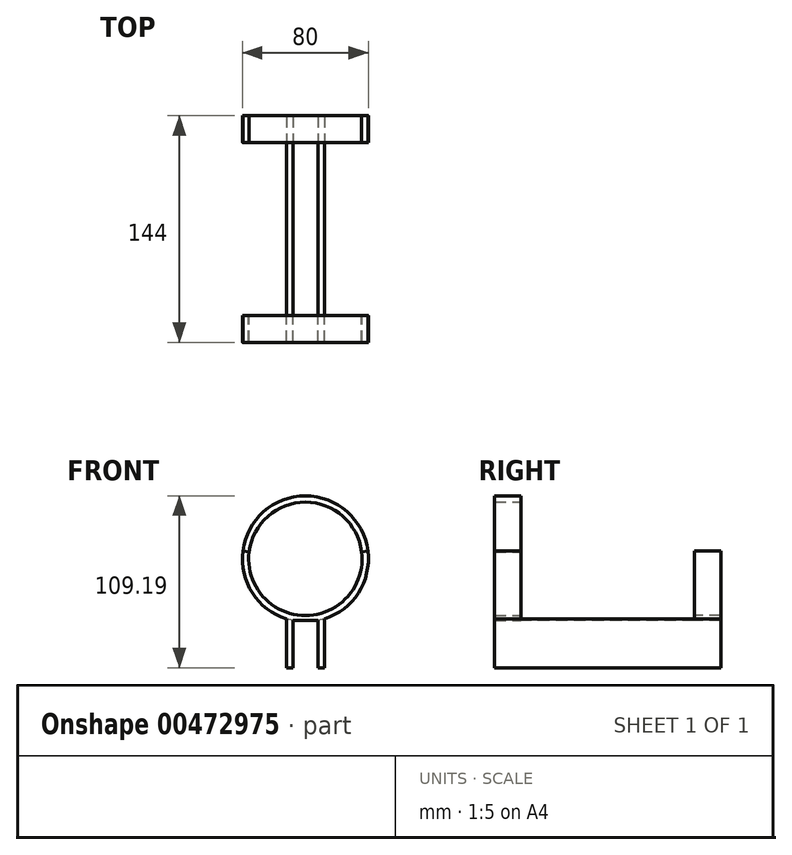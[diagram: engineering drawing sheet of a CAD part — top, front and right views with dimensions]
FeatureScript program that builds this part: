
annotation { "Feature Type Name" : "Feature", "Feature Type Description" : "" }
export const myFeature = defineFeature(function(context is Context, id is Id, definition is map)
    precondition{}
    {
        {
            var Q0;
            Q0=qCreatedBy(makeId("Front.planeOp"),FACE);
            var sketch = newSketch(context, id + "F0", { "sketchPlane" : qUnion([Q0])});
            skArc(sketch, "E0", {"start": v(-35.72, 4.5) * mm, "mid": v(0, -36) * mm, "end": v(35.72, 4.5) * mm});
            skArc(sketch, "E1.0", {"start": v(-39.69, 5) * mm, "mid": v(-33.67, -21.6) * mm, "end": v(-12, -38.16) * mm});
            skLineSegment(sketch, "E2", {"start": v(0, 47.34) * mm, "end": v(0, -79.2) * mm, "construction": true});
            skLineSegment(sketch, "E3", {"start": v(-35.72, 4.5) * mm, "end": v(-39.69, 5) * mm});
            skLineSegment(sketch, "E4.MirrorCS", {"start": v(35.72, 4.5) * mm, "end": v(39.69, 5) * mm});
            skLineSegment(sketch, "E5", {"start": v(8, -39.2) * mm, "end": v(8, -69.2) * mm});
            skLineSegment(sketch, "E6", {"start": v(8, -69.2) * mm, "end": v(12, -69.2) * mm});
            skLineSegment(sketch, "E7", {"start": v(12, -69.2) * mm, "end": v(12, -38.16) * mm});
            skLineSegment(sketch, "E8.MirrorCS", {"start": v(-8, -39.2) * mm, "end": v(-8, -69.2) * mm});
            skLineSegment(sketch, "E9.MirrorCS", {"start": v(-12, -69.2) * mm, "end": v(-12, -38.16) * mm});
            skLineSegment(sketch, "E10.MirrorCS", {"start": v(-8, -69.2) * mm, "end": v(-12, -69.2) * mm});
            skPoint(sketch, "E11.MirrorCS.start.orphan", {"position": v(0, -40) * mm});
            skArc(sketch, "E12.trimOffspring", {"start": v(12, -38.16) * mm, "mid": v(33.67, -21.6) * mm, "end": v(39.69, 5) * mm});
            skLineSegment(sketch, "E13", {"start": v(-8, -39.2) * mm, "end": v(8, -39.2) * mm});
            skArc(sketch, "E14", {"start": v(35.72, 4.5) * mm, "mid": v(0, 36) * mm, "end": v(-35.72, 4.5) * mm});
            skArc(sketch, "E15", {"start": v(39.69, 5) * mm, "mid": v(0, 40) * mm, "end": v(-39.69, 5) * mm});
            skSolve(sketch);
        }
        {
            var Q0;
            Q0=makeQuery(id+"F0.imprint","IMPRINT",FACE,{"disambiguationData":[TD([[makeQuery(id+"F0.imprint","IMPRINT",EDGE,{"derivedFrom":sQuery(id+"F0.wireOp",EDGE,"E0")}),-1.0]])]});
            var sketch = newSketch(context, id + "F1", { "sketchPlane" : qUnion([Q0])});
            skLineSegment(sketch, "E16.0.0", {"start": v(-8, -39.2) * mm, "end": v(8, -39.2) * mm});
            skLineSegment(sketch, "E16.0.1", {"start": v(8, -39.2) * mm, "end": v(8, -69.2) * mm});
            skLineSegment(sketch, "E16.0.2", {"start": v(8, -69.2) * mm, "end": v(12, -69.2) * mm});
            skLineSegment(sketch, "E16.0.3", {"start": v(12, -69.2) * mm, "end": v(12, -38.16) * mm});
            skArc(sketch, "E16.0.4", {"start": v(12, -38.16) * mm, "mid": v(33.67, -21.6) * mm, "end": v(39.69, 5) * mm});
            skLineSegment(sketch, "E16.0.5", {"start": v(39.69, 5) * mm, "end": v(35.72, 4.5) * mm});
            skArc(sketch, "E16.0.6", {"start": v(35.72, 4.5) * mm, "mid": v(0, -36) * mm, "end": v(-35.72, 4.5) * mm});
            skLineSegment(sketch, "E16.0.7", {"start": v(-35.72, 4.5) * mm, "end": v(-39.69, 5) * mm});
            skArc(sketch, "E16.0.8", {"start": v(-39.69, 5) * mm, "mid": v(-33.67, -21.6) * mm, "end": v(-12, -38.16) * mm});
            skLineSegment(sketch, "E16.0.9", {"start": v(-12, -38.16) * mm, "end": v(-12, -69.2) * mm});
            skLineSegment(sketch, "E16.0.10", {"start": v(-12, -69.2) * mm, "end": v(-8, -69.2) * mm});
            skLineSegment(sketch, "E16.0.11", {"start": v(-8, -69.2) * mm, "end": v(-8, -39.2) * mm});
            skSolve(sketch);
        }
        {
            var Q0;
            Q0 = qSketchRegion(id + "F1", true);
            var Q1;
            Q1=makeQuery(id+"F0.imprint","IMPRINT",FACE,{"disambiguationData":[TD([[makeQuery(id+"F0.imprint","IMPRINT",EDGE,{"derivedFrom":sQuery(id+"F0.wireOp",EDGE,"E3")}),-1.0]])]});
            extrude(context, id + "F2", {"entities" : qUnion([Q0, Q1]), "depth" : 17 * mm});
        }
        {
            var Q0;
            Q0=qCreatedBy(makeId("Front.planeOp"),FACE);
            var sketch = newSketch(context, id + "F3", { "sketchPlane" : qUnion([Q0])});
            skLineSegment(sketch, "E17.0", {"start": v(12, -69.2) * mm, "end": v(12, -38.16) * mm});
            skLineSegment(sketch, "E18.0", {"start": v(8, -39.2) * mm, "end": v(8, -69.2) * mm});
            skLineSegment(sketch, "E19.0", {"start": v(8, -69.2) * mm, "end": v(12, -69.2) * mm});
            skLineSegment(sketch, "E20.0", {"start": v(-8, -39.2) * mm, "end": v(-8, -69.2) * mm});
            skLineSegment(sketch, "E21.0", {"start": v(-8, -69.2) * mm, "end": v(-12, -69.2) * mm});
            skLineSegment(sketch, "E22.0", {"start": v(-12, -69.2) * mm, "end": v(-12, -38.16) * mm});
            skLineSegment(sketch, "E23", {"start": v(12, -38.16) * mm, "end": v(8, -39.2) * mm});
            skLineSegment(sketch, "E24", {"start": v(-8, -39.2) * mm, "end": v(-12, -38.16) * mm});
            skSolve(sketch);
        }
        {
            var Q0;
            Q0 = qSketchRegion(id + "F3", true);
            extrude(context, id + "F4", {"entities" : qUnion([Q0]), "operationType" : NewBodyOperationType.ADD, "oppositeDirection" : true, "depth" : 110 * mm});
        }
        {
            var Q0;
            Q0=qCreatedBy(makeId("Front.planeOp"),FACE);
            cPlane(context, id + "F5", {"entities" : qUnion([Q0]), "cplaneType" : CPlaneType.OFFSET, "offset" : 110 * mm, "oppositeDirection" : true, "width" : 150 * mm, "height" : 150 * mm});
        }
        {
            var Q0;
            Q0=qCreatedBy(id+"F5.planeOp",FACE);
            var sketch = newSketch(context, id + "F6", { "sketchPlane" : qUnion([Q0])});
            skLineSegment(sketch, "E25.0.0", {"start": v(-8, -39.2) * mm, "end": v(8, -39.2) * mm});
            skLineSegment(sketch, "E25.0.1", {"start": v(8, -39.2) * mm, "end": v(8, -69.2) * mm});
            skLineSegment(sketch, "E25.0.2", {"start": v(8, -69.2) * mm, "end": v(12, -69.2) * mm});
            skLineSegment(sketch, "E25.0.3", {"start": v(12, -69.2) * mm, "end": v(12, -38.16) * mm});
            skArc(sketch, "E25.0.4", {"start": v(12, -38.16) * mm, "mid": v(33.67, -21.6) * mm, "end": v(39.69, 5) * mm});
            skLineSegment(sketch, "E25.0.5", {"start": v(39.69, 5) * mm, "end": v(35.72, 4.5) * mm});
            skArc(sketch, "E25.0.6", {"start": v(35.72, 4.5) * mm, "mid": v(0, -36) * mm, "end": v(-35.72, 4.5) * mm});
            skLineSegment(sketch, "E25.0.7", {"start": v(-35.72, 4.5) * mm, "end": v(-39.69, 5) * mm});
            skArc(sketch, "E25.0.8", {"start": v(-39.69, 5) * mm, "mid": v(-33.67, -21.6) * mm, "end": v(-12, -38.16) * mm});
            skLineSegment(sketch, "E25.0.9", {"start": v(-12, -38.16) * mm, "end": v(-12, -69.2) * mm});
            skLineSegment(sketch, "E25.0.10", {"start": v(-12, -69.2) * mm, "end": v(-8, -69.2) * mm});
            skLineSegment(sketch, "E25.0.11", {"start": v(-8, -69.2) * mm, "end": v(-8, -39.2) * mm});
            skSolve(sketch);
        }
        {
            var Q0;
            Q0 = qSketchRegion(id + "F6", true);
            extrude(context, id + "F7", {"entities" : qUnion([Q0]), "operationType" : NewBodyOperationType.ADD, "oppositeDirection" : true, "depth" : 17 * mm});
        }
    });
